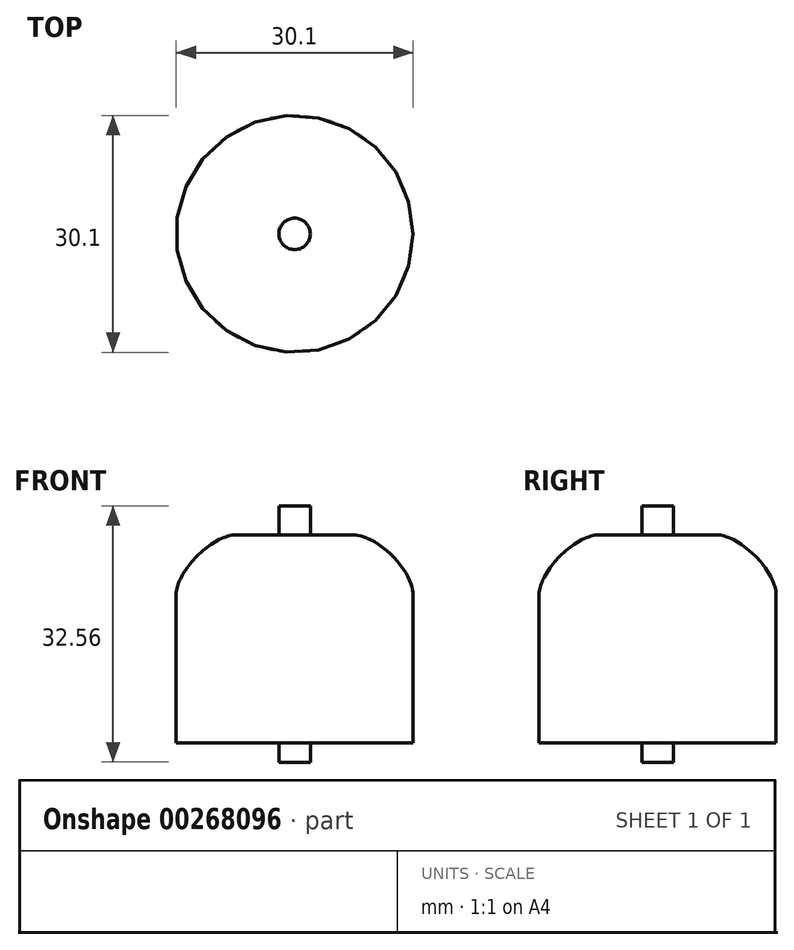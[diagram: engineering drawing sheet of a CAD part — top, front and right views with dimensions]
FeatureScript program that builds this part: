
annotation { "Feature Type Name" : "Feature", "Feature Type Description" : "" }
export const myFeature = defineFeature(function(context is Context, id is Id, definition is map)
    precondition{}
    {
        {
            var Q0;
            Q0=qCreatedBy(makeId("Top.planeOp"),FACE);
            var sketch = newSketch(context, id + "F0", { "sketchPlane" : qUnion([Q0])});
            skCircle(sketch, "E0", {"center": v(0, 0) * mm, "radius": 15.05 * mm});
            skSolve(sketch);
        }
        {
            var Q0;
            Q0 = qSketchRegion(id + "F0", true);
            extrude(context, id + "F1", {"entities" : qUnion([Q0]), "depth" : 26.42 * mm});
        }
        {
            var Q0;
            Q0=makeQuery(id+"F1.opExtrude","CAP_FACE",FACE,{"disambiguationData":[OSD([sQuery(id+"F0.wireOp",EDGE,"E0")])],"isStart":false});
            var sketch = newSketch(context, id + "F2", { "sketchPlane" : qUnion([Q0])});
            skCircle(sketch, "E1", {"center": v(0, 0) * mm, "radius": 2 * mm});
            skSolve(sketch);
        }
        {
            var Q0;
            Q0 = qSketchRegion(id + "F2", true);
            extrude(context, id + "F3", {"entities" : qUnion([Q0]), "operationType" : NewBodyOperationType.ADD, "depth" : 3.68 * mm});
        }
        {
            var Q0;
            Q0=makeQuery(id+"F1.opExtrude","CAP_FACE",FACE,{"disambiguationData":[OSD([sQuery(id+"F0.wireOp",EDGE,"E0")])],"isStart":true});
            var sketch = newSketch(context, id + "F4", { "sketchPlane" : qUnion([Q0])});
            skCircle(sketch, "E2", {"center": v(0, 0) * mm, "radius": 2 * mm});
            skSolve(sketch);
        }
        {
            var Q0;
            Q0 = qSketchRegion(id + "F4", true);
            extrude(context, id + "F5", {"entities" : qUnion([Q0]), "operationType" : NewBodyOperationType.ADD, "depth" : 2.46 * mm});
        }
        {
            var Q0;
            Q0=makeQuery(id+"F1.opExtrude","CAP_EDGE",EDGE,{"disambiguationData":[OSD([sQuery(id+"F0.wireOp",EDGE,"E0")])],"isStart":false});
            fillet(context, id + "F6", {"entities" : qUnion([Q0]), "radius" : 7.62 * mm, "tangentPropagation" : true, "rho" : .3, "crossSection" : FilletCrossSection.CONIC, "allowEdgeOverflow" : false});
        }
    });
